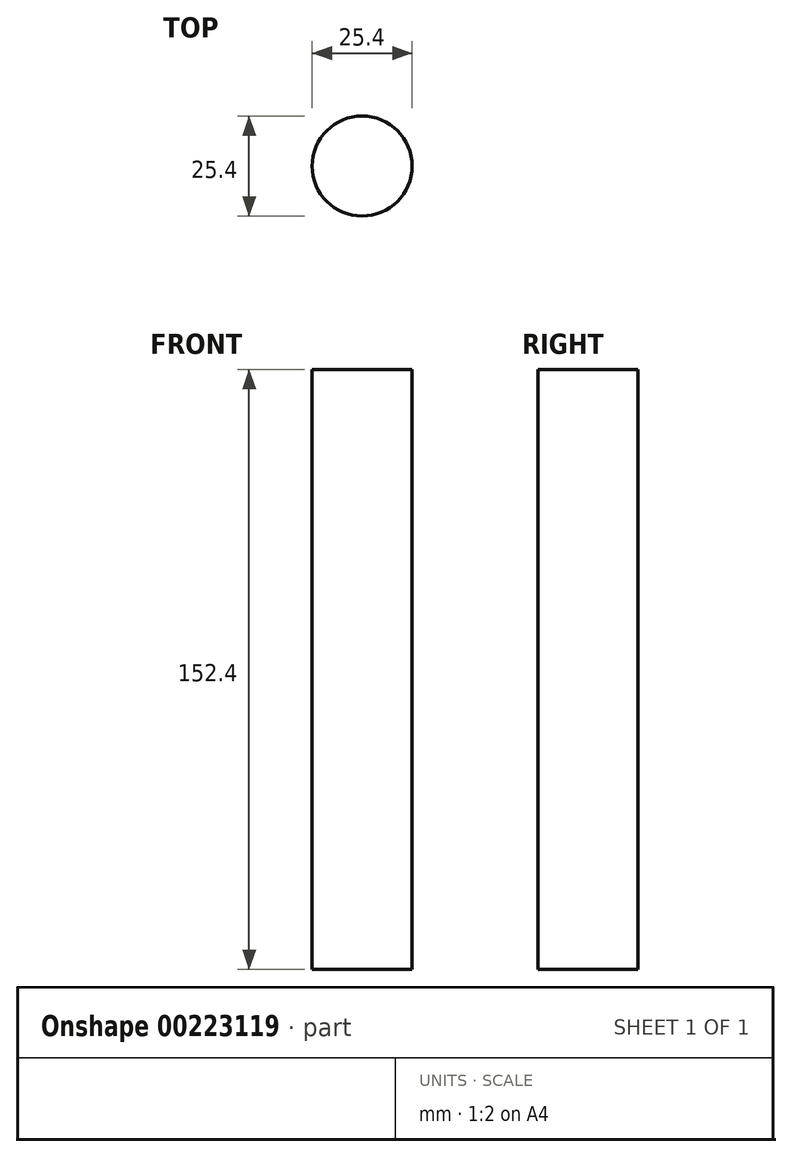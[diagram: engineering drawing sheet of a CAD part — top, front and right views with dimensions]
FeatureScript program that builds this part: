
annotation { "Feature Type Name" : "Feature", "Feature Type Description" : "" }
export const myFeature = defineFeature(function(context is Context, id is Id, definition is map)
    precondition{}
    {
        {
            var Q0;
            Q0=qCreatedBy(makeId("Top.planeOp"),FACE);
            var sketch = newSketch(context, id + "F0", { "sketchPlane" : qUnion([Q0])});
            skCircle(sketch, "E0", {"center": v(0, 0) * mm, "radius": 12.7 * mm});
            skSolve(sketch);
        }
        {
            var Q0;
            Q0 = qSketchRegion(id + "F0", true);
            extrude(context, id + "F1", {"entities" : qUnion([Q0]), "oppositeDirection" : true, "depth" : 152.4 * mm});
        }
    });
